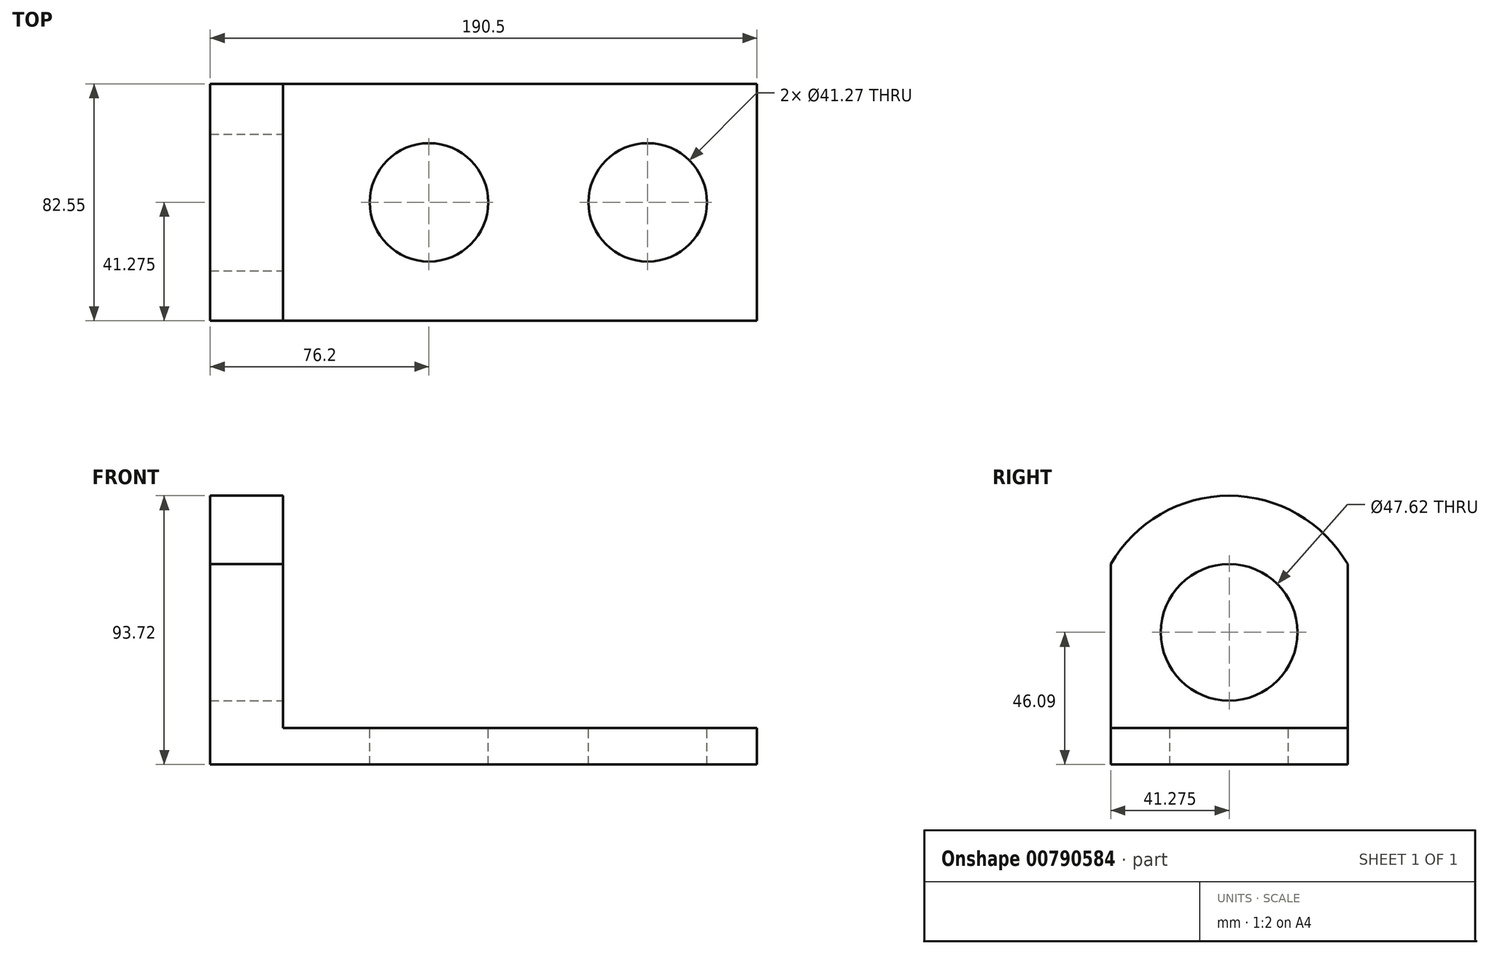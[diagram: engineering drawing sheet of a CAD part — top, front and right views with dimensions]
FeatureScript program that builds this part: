
annotation { "Feature Type Name" : "Feature", "Feature Type Description" : "" }
export const myFeature = defineFeature(function(context is Context, id is Id, definition is map)
    precondition{}
    {
        {
            var Q0;
            Q0=qCreatedBy(makeId("Front.planeOp"),FACE);
            var sketch = newSketch(context, id + "F0", { "sketchPlane" : qUnion([Q0])});
            skLineSegment(sketch, "E0", {"start": v(0, 0) * mm, "end": v(190.5, 0) * mm});
            skLineSegment(sketch, "E1", {"start": v(0, 0) * mm, "end": v(0, 101.6) * mm});
            skLineSegment(sketch, "E2", {"start": v(0, 101.6) * mm, "end": v(25.4, 101.6) * mm});
            skLineSegment(sketch, "E3", {"start": v(25.4, 101.6) * mm, "end": v(25.4, 12.7) * mm});
            skLineSegment(sketch, "E4", {"start": v(25.4, 12.7) * mm, "end": v(190.5, 12.7) * mm});
            skLineSegment(sketch, "E5", {"start": v(190.5, 12.7) * mm, "end": v(190.5, 0) * mm});
            skSolve(sketch);
        }
        {
            var Q0;
            Q0=makeQuery(id+"F0.imprint","IMPRINT",FACE,{"disambiguationData":[TD([[makeQuery(id+"F0.imprint","IMPRINT",EDGE,{"derivedFrom":sQuery(id+"F0.wireOp",EDGE,"E0")}),1.0]])]});
            extrude(context, id + "F1", {"entities" : qUnion([Q0]), "depth" : 82.55 * mm, "offsetDistance" : 25.4 * mm});
        }
        {
            var Q0;
            Q0=makeQuery(id+"F1.opExtrude","SWEPT_FACE",FACE,{"disambiguationData":[OSD([sQuery(id+"F0.wireOp",EDGE,"E4")])]});
            var sketch = newSketch(context, id + "F2", { "sketchPlane" : qUnion([Q0])});
            skLineSegment(sketch, "E6", {"start": v(190.5, -41.28) * mm, "end": v(152.4, -41.28) * mm, "construction": true});
            skLineSegment(sketch, "E7", {"start": v(152.4, -41.28) * mm, "end": v(76.2, -41.28) * mm, "construction": true});
            skCircle(sketch, "E8", {"center": v(76.2, -41.28) * mm, "radius": 20.64 * mm});
            skCircle(sketch, "E9", {"center": v(152.4, -41.28) * mm, "radius": 20.64 * mm});
            skSolve(sketch);
        }
        {
            var Q0;
            Q0=makeQuery(id+"F2.imprint","IMPRINT",FACE,{"disambiguationData":[TD([[makeQuery(id+"F2.imprint","IMPRINT",EDGE,{"derivedFrom":sQuery(id+"F2.wireOp",EDGE,"E8")}),1.0]])]});
            var Q1;
            Q1=makeQuery(id+"F2.imprint","IMPRINT",FACE,{"disambiguationData":[TD([[makeQuery(id+"F2.imprint","IMPRINT",EDGE,{"derivedFrom":sQuery(id+"F2.wireOp",EDGE,"E9")}),1.0]])]});
            extrude(context, id + "F3", {"entities" : qUnion([Q0, Q1]), "operationType" : NewBodyOperationType.REMOVE, "endBound" : BoundingType.THROUGH_ALL, "oppositeDirection" : true, "depth" : 25.4 * mm, "offsetDistance" : 25.4 * mm});
        }
        {
            var Q0;
            Q0=makeQuery(id+"F1.opExtrude","SWEPT_FACE",FACE,{"disambiguationData":[OSD([sQuery(id+"F0.wireOp",EDGE,"E3")])]});
            var sketch = newSketch(context, id + "F4", { "sketchPlane" : qUnion([Q0])});
            skLineSegment(sketch, "E10", {"start": v(-82.55, 12.7) * mm, "end": v(-82.55, 69.85) * mm});
            skLineSegment(sketch, "E11", {"start": v(0, 12.7) * mm, "end": v(0, 69.85) * mm});
            skArc(sketch, "E12", {"start": v(0, 69.85) * mm, "mid": v(-41.28, 93.72) * mm, "end": v(-82.55, 69.85) * mm});
            skSolve(sketch);
        }
        {
            var Q0;
            {var subQ0=sQuery(id+"F4.wireOp",EDGE,"E12");Q0=makeQuery(id+"F4.imprint","IMPRINT",FACE,{"disambiguationData":[TD([[makeQuery(id+"F4.imprint","IMPRINT",EDGE,{"derivedFrom":subQ0}),-1.0]])]});}
            extrude(context, id + "F5", {"entities" : qUnion([Q0]), "operationType" : NewBodyOperationType.REMOVE, "endBound" : BoundingType.THROUGH_ALL, "oppositeDirection" : true, "depth" : 25.4 * mm, "offsetDistance" : 25.4 * mm});
        }
        {
            var Q0;
            Q0=makeQuery(id+"F1.opExtrude","SWEPT_FACE",FACE,{"disambiguationData":[OSD([sQuery(id+"F0.wireOp",EDGE,"E3")])]});
            var sketch = newSketch(context, id + "F6", { "sketchPlane" : qUnion([Q0])});
            skLineSegment(sketch, "E13", {"start": v(-41.28, 93.72) * mm, "end": v(-41.27, 46.1) * mm, "construction": true});
            skCircle(sketch, "E14", {"center": v(-41.27, 46.1) * mm, "radius": 23.81 * mm});
            skSolve(sketch);
        }
        {
            var Q0;
            Q0=makeQuery(id+"F6.imprint","IMPRINT",FACE,{"disambiguationData":[TD([[makeQuery(id+"F6.imprint","IMPRINT",EDGE,{"derivedFrom":sQuery(id+"F6.wireOp",EDGE,"E14")}),1.0]])]});
            extrude(context, id + "F7", {"entities" : qUnion([Q0]), "operationType" : NewBodyOperationType.REMOVE, "endBound" : BoundingType.THROUGH_ALL, "oppositeDirection" : true, "depth" : 25.4 * mm, "offsetDistance" : 25.4 * mm});
        }
    });
